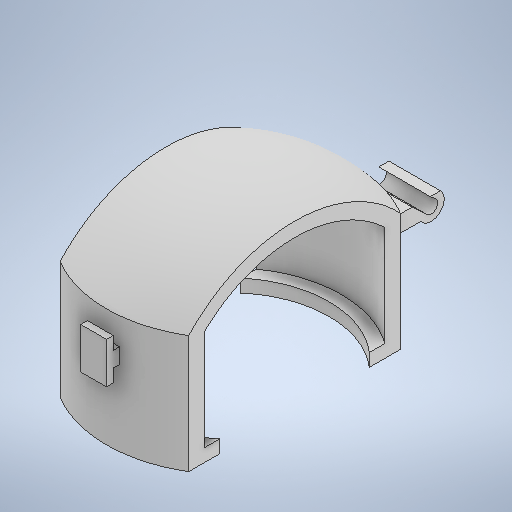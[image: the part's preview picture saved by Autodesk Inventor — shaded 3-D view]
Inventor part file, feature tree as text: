
AUTODESK INVENTOR PART (.ipt)
format: ipt  version: 2025 (Build 290162010, 162A)  size: 322,560 bytes
history: native  units: in
note: dims shown in document units (in); Inventor stores cm internally (conversion verified against a paired STEP export)
features: sketch x4, extrude x3, revolve x1
ambient origin geometry x8: Origin, YZ Plane, XZ Plane, XY Plane, X Axis, Y Axis, Z Axis, Center Point
bodies: Body1 (feature_tree)
feature tree (8):
  revolve  "Revolution1"  [1 undecoded]
  extrude  "Extrusion2"  Depth=0.25in
  extrude  "Extrusion3"  TaperAngle=360.0deg  [1 undecoded]
  extrude  "Extrusion4"  Depth=1.0in TaperAngle=0.0deg
  sketch  "Sketch3"  dims[d7=4.31in d9=2.95in]
  sketch  "Sketch4"  dims[d10=1.95in d11=0.25in]
  sketch  "Sketch5"  dims[d13=0.24in d14=360.0deg]
  sketch  "Sketch6"  dims[d15=2.5in d16=1.0in d17=0.0in d18=0.3in d19=1.0in d20=0.25in d21=0.5in d22=0.3436in d23=1.0in d24=0.0in d25=0.8in d26=0.25in d27=0.25in d28=0.12in d29=0.25in d30=0.12in d31=0.5in d32=0.0in]
note: 2 required parameter values undecoded (feature->parameter linkage not recoverable at this tier; creation-order binding heuristic only, values carry confidence <= 0.55)